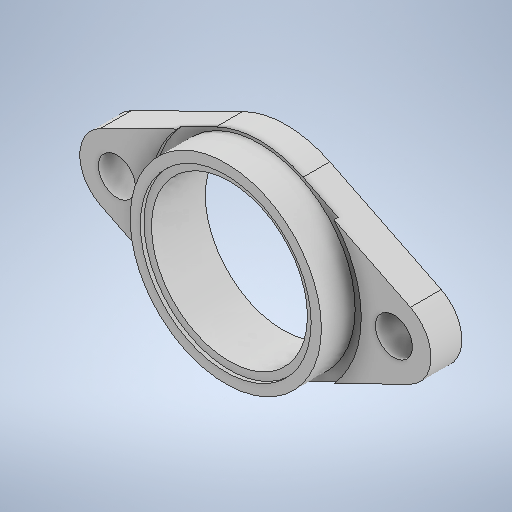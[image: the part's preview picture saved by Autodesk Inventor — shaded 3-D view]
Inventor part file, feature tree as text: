
AUTODESK INVENTOR PART (.ipt)
format: ipt  version: 2025.2 (Build 292293000, 293)  size: 515,072 bytes
history: native  units: mm
features: extrude x5, projected_geometry x2, emboss x1, sketch x1
ambient origin geometry x8: Origin, YZ Plane, XZ Plane, XY Plane, X Axis, Y Axis, Z Axis, Center Point
bodies: Solid1 (feature_tree)
feature tree (9):
  extrude  "Extrusion1"  Depth=0.5mm
  extrude  "Extrusion2"  Depth=0.5mm
  extrude  "Extrusion3"  Depth=0.5mm
  emboss  "Emboss1"
  extrude  "Extrusion4"  Depth=0.5mm
  extrude  "Extrusion5"  Depth=0.5mm TaperAngle=0.0deg
  projected_geometry  "Projected Loop1"
  sketch  "Sketch4"  dims[d0=47.3mm d1=26.5mm d2=5.0mm d3=2.5mm d4=21.0mm d5=4.15mm d6=0.0mm d7=28.5mm d8=0.55mm d9=0.0mm d10=1.5mm d11=2.0mm d13=3.0mm d15=0.6mm d16=0.4mm d17=0.0mm d18=1.5mm d19=1.0mm d20=1.5mm d21=0.4mm d22=0.0mm d24=25.75mm d25=4.55mm d26=0.0mm d27=23.0mm d28=0.5mm d29=0.0mm]
  projected_geometry  "Projected Loop2"
